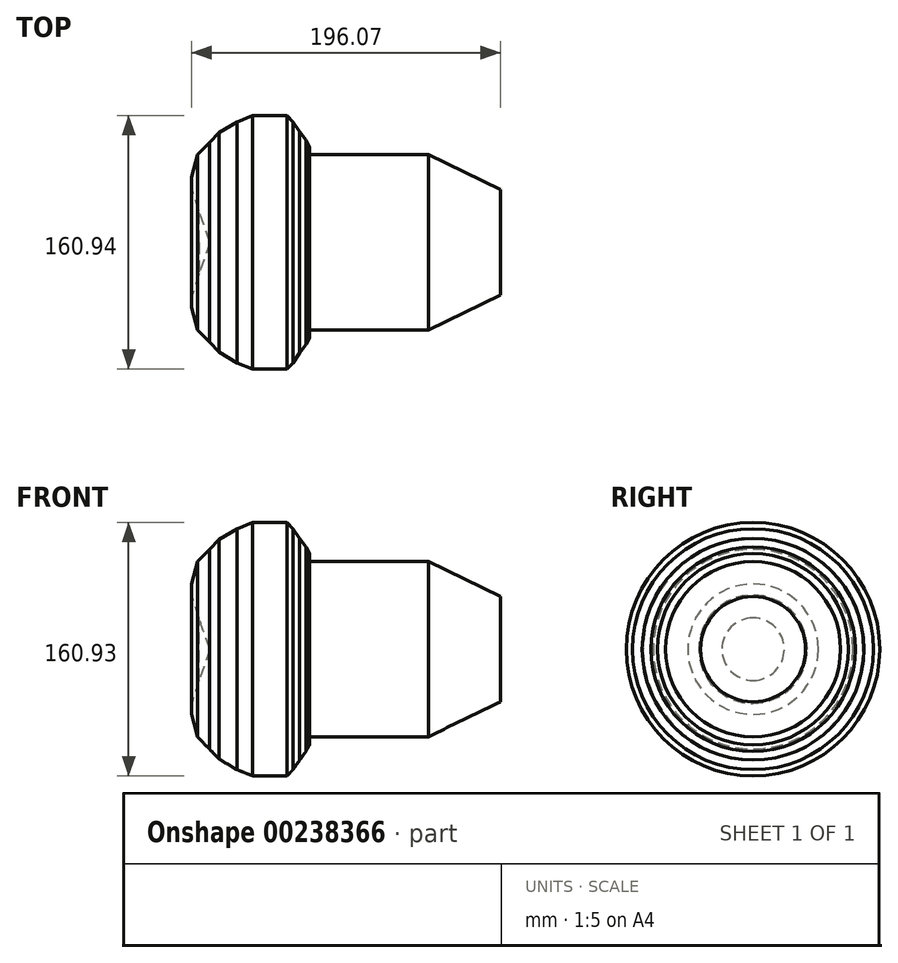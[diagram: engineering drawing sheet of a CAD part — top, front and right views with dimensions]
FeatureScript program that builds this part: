
annotation { "Feature Type Name" : "Feature", "Feature Type Description" : "" }
export const myFeature = defineFeature(function(context is Context, id is Id, definition is map)
    precondition{}
    {
        {
            var Q0;
            Q0=qCreatedBy(makeId("Front.planeOp"),FACE);
            var sketch = newSketch(context, id + "F0", { "sketchPlane" : qUnion([Q0])});
            skLineSegment(sketch, "E0", {"start": v(0, 0) * mm, "end": v(45.8, 22.22) * mm});
            skLineSegment(sketch, "E1", {"start": v(45.8, 22.22) * mm, "end": v(45.8, 55.63) * mm});
            skLineSegment(sketch, "E2", {"start": v(45.8, 55.63) * mm, "end": v(-100.58, 55.63) * mm});
            skLineSegment(sketch, "E3", {"start": v(-100.58, 55.63) * mm, "end": v(-138.68, 55.63) * mm});
            skLineSegment(sketch, "E4", {"start": v(-138.68, 55.63) * mm, "end": v(-145.7, 35.81) * mm});
            skLineSegment(sketch, "E5", {"start": v(-145.7, 35.81) * mm, "end": v(-150.27, 21.18) * mm});
            skLineSegment(sketch, "E6", {"start": v(-150.27, 21.18) * mm, "end": v(-150.27, 14.17) * mm});
            skLineSegment(sketch, "E7", {"start": v(-150.27, 14.17) * mm, "end": v(-146.6, 0) * mm});
            skLineSegment(sketch, "E8", {"start": v(-146.6, 0) * mm, "end": v(-138.99, -7.77) * mm});
            skLineSegment(sketch, "E9", {"start": v(-138.99, -7.77) * mm, "end": v(-132.9, -14.17) * mm});
            skLineSegment(sketch, "E10", {"start": v(-132.9, -14.17) * mm, "end": v(-121.62, -20.88) * mm});
            skLineSegment(sketch, "E11", {"start": v(-121.62, -20.88) * mm, "end": v(-111.56, -24.84) * mm});
            skLineSegment(sketch, "E12", {"start": v(-111.56, -24.84) * mm, "end": v(-100.89, -24.84) * mm});
            skLineSegment(sketch, "E13", {"start": v(-100.89, -24.84) * mm, "end": v(-89.61, -24.84) * mm});
            skLineSegment(sketch, "E14", {"start": v(-89.61, -24.84) * mm, "end": v(-85.95, -20.88) * mm});
            skLineSegment(sketch, "E15", {"start": v(-85.95, -20.88) * mm, "end": v(-81.69, -14.78) * mm});
            skLineSegment(sketch, "E16", {"start": v(-81.69, -14.78) * mm, "end": v(-77.72, -9.3) * mm});
            skLineSegment(sketch, "E17", {"start": v(-77.72, -9.3) * mm, "end": v(-75.29, -5.03) * mm});
            skLineSegment(sketch, "E18", {"start": v(-75.29, -5.03) * mm, "end": v(-75.29, 0) * mm});
            skLineSegment(sketch, "E19", {"start": v(-75.29, 0) * mm, "end": v(0, 0) * mm});
            skSolve(sketch);
        }
        {
            var Q0;
            Q0=makeQuery(id+"F0.imprint","IMPRINT",FACE,{"disambiguationData":[TD([[makeQuery(id+"F0.imprint","IMPRINT",EDGE,{"derivedFrom":sQuery(id+"F0.wireOp",EDGE,"E0")}),1.0]])]});
            var Q1;
            Q1=sQuery(id+"F0.wireOp",EDGE,"E2");
            revolve(context, id + "F1", {"entities" : qUnion([Q0]), "axis" : qUnion([Q1]), "revolveType" : RevolveType.FULL});
        }
    });
